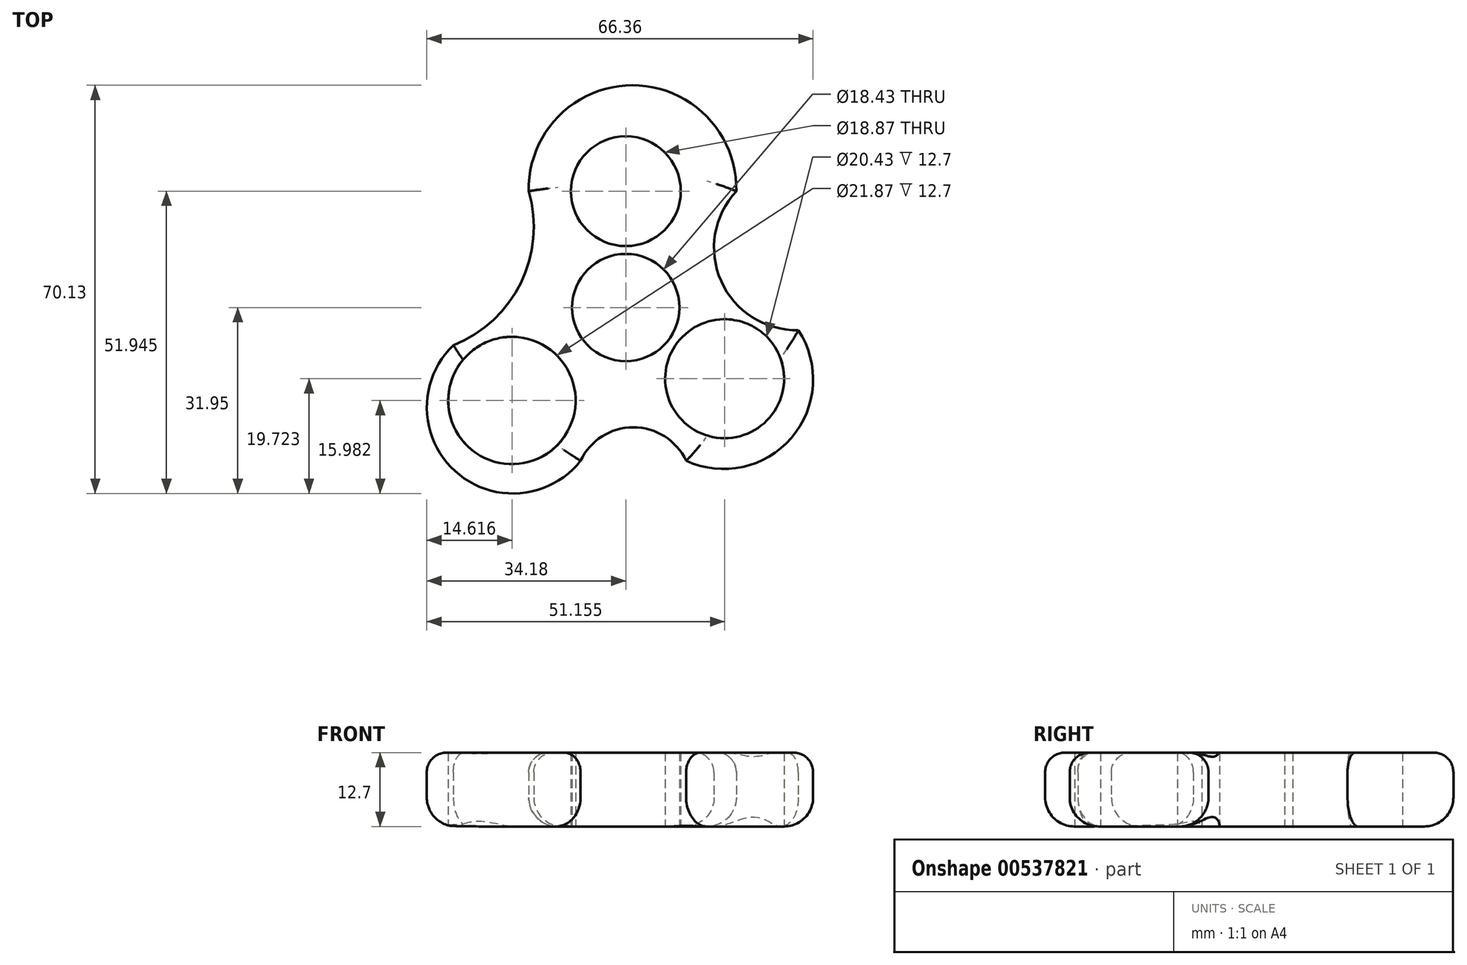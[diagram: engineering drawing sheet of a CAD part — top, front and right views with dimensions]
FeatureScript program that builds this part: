
annotation { "Feature Type Name" : "Feature", "Feature Type Description" : "" }
export const myFeature = defineFeature(function(context is Context, id is Id, definition is map)
    precondition{}
    {
        {
            var Q0;
            Q0=qCreatedBy(makeId("Top.planeOp"),FACE);
            var sketch = newSketch(context, id + "F0", { "sketchPlane" : qUnion([Q0])});
            skCircle(sketch, "E0", {"center": v(0, 0) * mm, "radius": 9.22 * mm});
            skCircle(sketch, "E1", {"center": v(0, 20) * mm, "radius": 9.44 * mm});
            skCircle(sketch, "E2", {"center": v(16.97, -12.23) * mm, "radius": 10.22 * mm});
            skCircle(sketch, "E3", {"center": v(-19.56, -15.97) * mm, "radius": 10.94 * mm});
            skArc(sketch, "E4", {"start": v(-29.63, -6.47) * mm, "mid": v(-29.33, -28.1) * mm, "end": v(-7.77, -26.32) * mm});
            skArc(sketch, "E5", {"start": v(18.99, 20) * mm, "mid": v(1.15, 38.18) * mm, "end": v(-16.69, 20) * mm});
            skArc(sketch, "E6", {"start": v(10.36, -26.32) * mm, "mid": v(28.46, -22.38) * mm, "end": v(29.63, -3.88) * mm});
            skArc(sketch, "E7", {"start": v(10.36, -26.32) * mm, "mid": v(1.3, -20.57) * mm, "end": v(-7.77, -26.32) * mm});
            skArc(sketch, "E8", {"start": v(-29.63, -6.47) * mm, "mid": v(-18.03, 4.25) * mm, "end": v(-16.69, 20) * mm});
            skArc(sketch, "E9", {"start": v(18.99, 20) * mm, "mid": v(16.38, 4.52) * mm, "end": v(29.63, -3.88) * mm});
            skSolve(sketch);
        }
        {
            var Q0;
            Q0=makeQuery(id+"F0.imprint","IMPRINT",FACE,{"disambiguationData":[TD([[makeQuery(id+"F0.imprint","IMPRINT",EDGE,{"derivedFrom":sQuery(id+"F0.wireOp",EDGE,"E0")}),-1.0]])]});
            extrude(context, id + "F1", {"entities" : qUnion([Q0]), "depth" : 12.7 * mm, "offsetDistance" : 25 * mm});
        }
        {
            var Q0;
            Q0=makeQuery(id+"F1.opExtrude","CAP_EDGE",EDGE,{"disambiguationData":[OSD([sQuery(id+"F0.wireOp",EDGE,"E4")])],"isStart":false});
            var Q1;
            Q1=makeQuery(id+"F1.opExtrude","CAP_EDGE",EDGE,{"disambiguationData":[OSD([sQuery(id+"F0.wireOp",EDGE,"E8")])],"isStart":false});
            var Q2;
            Q2=makeQuery(id+"F1.opExtrude","CAP_EDGE",EDGE,{"disambiguationData":[OSD([sQuery(id+"F0.wireOp",EDGE,"E5")])],"isStart":false});
            var Q3;
            Q3=makeQuery(id+"F1.opExtrude","CAP_EDGE",EDGE,{"disambiguationData":[OSD([sQuery(id+"F0.wireOp",EDGE,"E9")])],"isStart":false});
            var Q4;
            Q4=makeQuery(id+"F1.opExtrude","CAP_EDGE",EDGE,{"disambiguationData":[OSD([sQuery(id+"F0.wireOp",EDGE,"E6")])],"isStart":false});
            var Q5;
            Q5=makeQuery(id+"F1.opExtrude","CAP_EDGE",EDGE,{"disambiguationData":[OSD([sQuery(id+"F0.wireOp",EDGE,"E7")])],"isStart":false});
            fillet(context, id + "F2", {"entities" : qUnion([Q0, Q1, Q2, Q3, Q4, Q5]), "radius" : 3.38 * mm, "tangentPropagation" : true, "allowEdgeOverflow" : false});
        }
        {
            var Q0;
            Q0=makeQuery(id+"F1.opExtrude","CAP_EDGE",EDGE,{"disambiguationData":[OSD([sQuery(id+"F0.wireOp",EDGE,"E9")])],"isStart":true});
            var Q1;
            Q1=makeQuery(id+"F1.opExtrude","CAP_EDGE",EDGE,{"disambiguationData":[OSD([sQuery(id+"F0.wireOp",EDGE,"E5")])],"isStart":true});
            var Q2;
            Q2=makeQuery(id+"F1.opExtrude","CAP_EDGE",EDGE,{"disambiguationData":[OSD([sQuery(id+"F0.wireOp",EDGE,"E8")])],"isStart":true});
            var Q3;
            Q3=makeQuery(id+"F1.opExtrude","CAP_EDGE",EDGE,{"disambiguationData":[OSD([sQuery(id+"F0.wireOp",EDGE,"E4")])],"isStart":true});
            var Q4;
            Q4=makeQuery(id+"F1.opExtrude","CAP_EDGE",EDGE,{"disambiguationData":[OSD([sQuery(id+"F0.wireOp",EDGE,"E7")])],"isStart":true});
            var Q5;
            Q5=makeQuery(id+"F1.opExtrude","CAP_EDGE",EDGE,{"disambiguationData":[OSD([sQuery(id+"F0.wireOp",EDGE,"E6")])],"isStart":true});
            fillet(context, id + "F3", {"entities" : qUnion([Q0, Q1, Q2, Q3, Q4, Q5]), "radius" : 5 * mm, "tangentPropagation" : true, "allowEdgeOverflow" : false});
        }
    });
